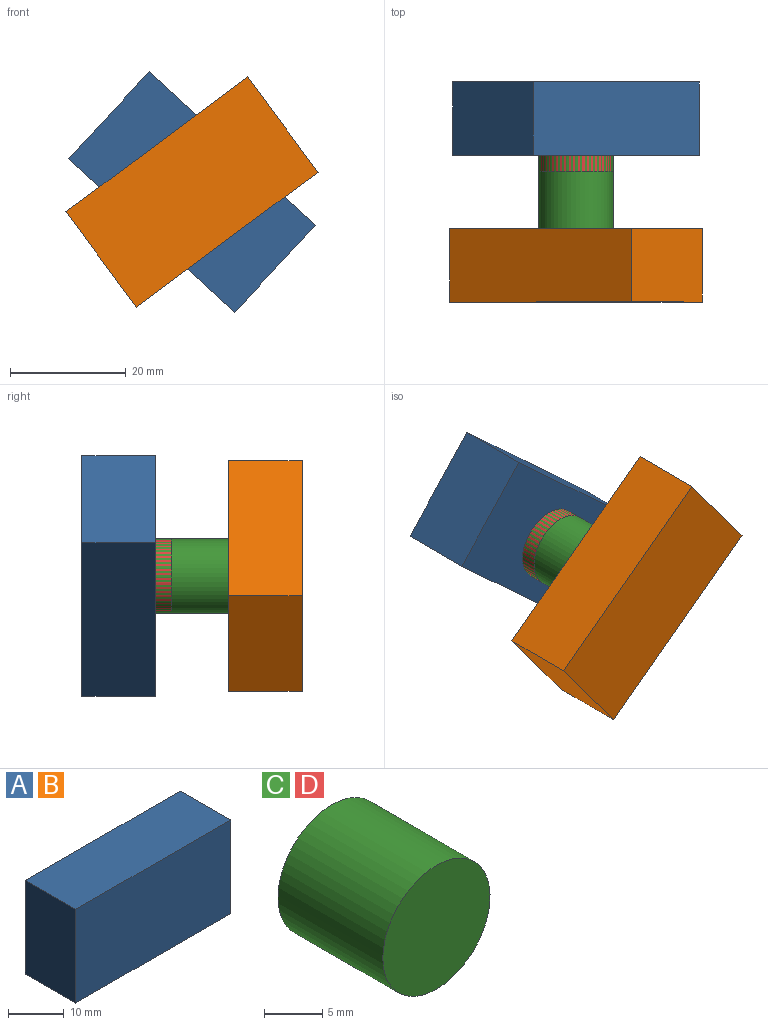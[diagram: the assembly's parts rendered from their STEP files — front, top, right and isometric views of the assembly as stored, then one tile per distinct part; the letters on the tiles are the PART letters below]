
ASSEMBLY  parts=4 mates=3
PART A: 6 faces, bbox 39.2x12.7x20.5 mm
  f0: plane 20.51x12.7mm, normal (-1,0,0), area 260.4mm2, adj f1,f3,f4,f5
  f1: plane 39.15x12.7mm, normal (0,0,-1), area 497.2mm2, adj f0,f2,f4,f5
  f2: plane 20.51x12.7mm, normal (1,0,0), area 260.4mm2, adj f1,f3,f4,f5
  f3: plane 39.15x12.7mm, normal (0,0,1), area 497.2mm2, adj f0,f2,f4,f5
  f4: plane 39.15x20.51mm, normal (0,-1,0), area 802.9mm2, adj f0,f1,f2,f3
  f5: plane 39.15x20.51mm, normal (0,1,0), area 802.9mm2, adj f0,f1,f2,f3
PART B: same geometry as A
PART C: 3 faces, bbox 13x12.7x13 mm
  f0: cylinder r=6.49mm len=12.98mm, axis (0,1,0), area 517.8mm2, adj f1,f2
  f1: plane 12.98x12.98mm, normal (0,-1,0), area 132.3mm2, adj f0
  f2: plane 12.98x12.98mm, normal (0,1,0), area 132.3mm2, adj f0
PART D: same geometry as C
PLACE A rot(axis=(-0.36,0,-0.93),180deg) t=(-95.05,0,50.46)mm
PLACE B rot(axis=(-0.31,0,0.95),180deg) t=(-18.78,-25.4,-17.64)mm
PLACE C rot(axis=(0,1,0),3.1deg) t=(-3.36,0,-0.76)mm fixed
PLACE D rot(axis=(0,-1,0),47.2deg) t=(40.64,9.9,31.68)mm
MATE slider A.f4 <-> D.f0  axis (0,1,0) through (-15.91,12.7,62.33)mm
MATE revolute C.f0 <-> A.f5  axis (0,1,0) through (-15.91,0,62.33)mm
MATE revolute B.f4 <-> C.f0  axis (0,-1,0) through (-15.91,-12.7,62.33)mm
